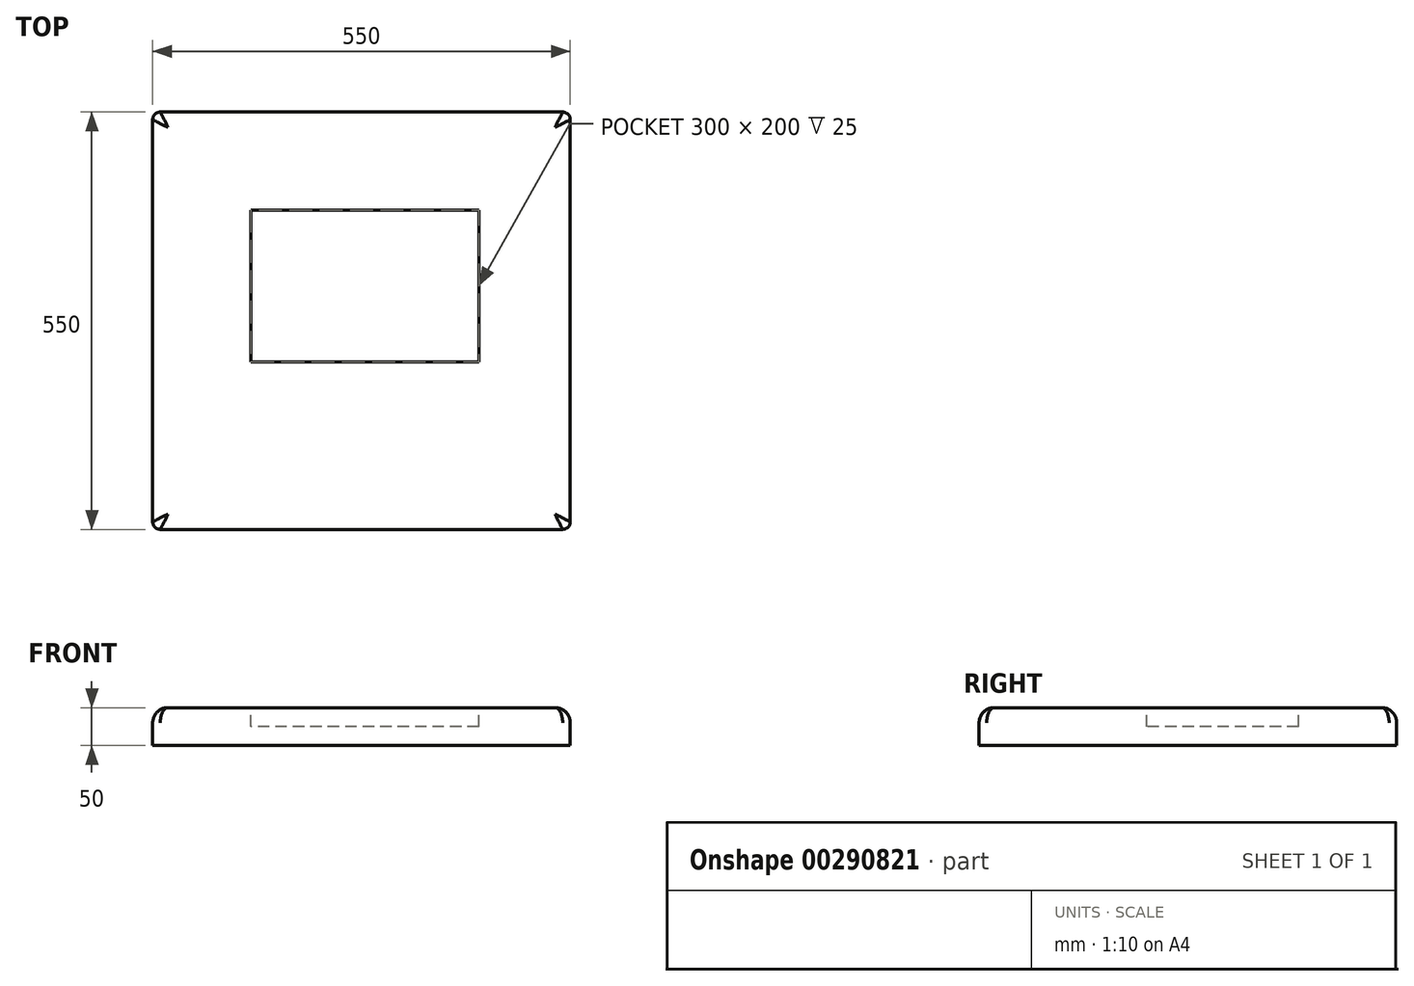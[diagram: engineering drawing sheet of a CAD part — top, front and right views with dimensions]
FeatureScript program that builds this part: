
annotation { "Feature Type Name" : "Feature", "Feature Type Description" : "" }
export const myFeature = defineFeature(function(context is Context, id is Id, definition is map)
    precondition{}
    {
        {
            var Q0;
            Q0=qCreatedBy(makeId("Top.planeOp"),FACE);
            var sketch = newSketch(context, id + "F0", { "sketchPlane" : qUnion([Q0])});
            skLineSegment(sketch, "E0.bottom", {"start": v(-279.6, 410.09) * mm, "end": v(270.4, 410.09) * mm});
            skLineSegment(sketch, "E0.top", {"start": v(-279.6, -139.91) * mm, "end": v(270.4, -139.91) * mm});
            skLineSegment(sketch, "E0.left", {"start": v(-279.6, 410.09) * mm, "end": v(-279.6, -139.91) * mm});
            skLineSegment(sketch, "E0.right", {"start": v(270.4, 410.09) * mm, "end": v(270.4, -139.91) * mm});
            skSolve(sketch);
        }
        {
            var Q0;
            Q0=makeQuery(id+"F0.imprint","IMPRINT",FACE,{"disambiguationData":[TD([[makeQuery(id+"F0.imprint","IMPRINT",EDGE,{"derivedFrom":sQuery(id+"F0.wireOp",EDGE,"E0.bottom")}),-1.0]])]});
            extrude(context, id + "F1", {"entities" : qUnion([Q0]), "depth" : 50 * mm});
        }
        {
            var Q0;
            Q0=makeQuery(id+"F1.opExtrude","CAP_EDGE",EDGE,{"disambiguationData":[OSD([sQuery(id+"F0.wireOp",EDGE,"E0.top")])],"isStart":false});
            var Q1;
            Q1=makeQuery(id+"F1.opExtrude","CAP_EDGE",EDGE,{"disambiguationData":[OSD([sQuery(id+"F0.wireOp",EDGE,"E0.left")])],"isStart":false});
            var Q2;
            Q2=makeQuery(id+"F1.opExtrude","CAP_EDGE",EDGE,{"disambiguationData":[OSD([sQuery(id+"F0.wireOp",EDGE,"E0.bottom")])],"isStart":false});
            var Q3;
            Q3=makeQuery(id+"F1.opExtrude","CAP_EDGE",EDGE,{"disambiguationData":[OSD([sQuery(id+"F0.wireOp",EDGE,"E0.right")])],"isStart":false});
            fillet(context, id + "F2", {"entities" : qUnion([Q0, Q1, Q2, Q3]), "radius" : 20 * mm, "tangentPropagation" : true, "allowEdgeOverflow" : false});
        }
        {
            var Q0;
            Q0=makeQuery(id+"F1.opExtrude","SWEPT_EDGE",EDGE,{"disambiguationData":[OSD([sQuery(id+"F0.wireOp",EDGE,"E0.bottom"),sQuery(id+"F0.wireOp",EDGE,"E0.right")])]});
            var Q1;
            Q1=makeQuery(id+"F2.opFillet","BLEND_EDGE",EDGE,{"blendedFrom":[makeQuery(id+"F1.opExtrude","CAP_EDGE",EDGE,{"disambiguationData":[OSD([sQuery(id+"F0.wireOp",EDGE,"E0.bottom")])],"isStart":false}),makeQuery(id+"F1.opExtrude","CAP_EDGE",EDGE,{"disambiguationData":[OSD([sQuery(id+"F0.wireOp",EDGE,"E0.right")])],"isStart":false})],"blendedInto":[]});
            var Q2;
            Q2=makeQuery(id+"F1.opExtrude","SWEPT_EDGE",EDGE,{"disambiguationData":[OSD([sQuery(id+"F0.wireOp",EDGE,"E0.top"),sQuery(id+"F0.wireOp",EDGE,"E0.right")])]});
            var Q3;
            Q3=makeQuery(id+"F2.opFillet","BLEND_EDGE",EDGE,{"blendedFrom":[makeQuery(id+"F1.opExtrude","CAP_EDGE",EDGE,{"disambiguationData":[OSD([sQuery(id+"F0.wireOp",EDGE,"E0.top")])],"isStart":false}),makeQuery(id+"F1.opExtrude","CAP_EDGE",EDGE,{"disambiguationData":[OSD([sQuery(id+"F0.wireOp",EDGE,"E0.right")])],"isStart":false})],"blendedInto":[]});
            var Q4;
            Q4=makeQuery(id+"F1.opExtrude","SWEPT_EDGE",EDGE,{"disambiguationData":[OSD([sQuery(id+"F0.wireOp",EDGE,"E0.top"),sQuery(id+"F0.wireOp",EDGE,"E0.left")])]});
            var Q5;
            Q5=makeQuery(id+"F2.opFillet","BLEND_EDGE",EDGE,{"blendedFrom":[makeQuery(id+"F1.opExtrude","CAP_EDGE",EDGE,{"disambiguationData":[OSD([sQuery(id+"F0.wireOp",EDGE,"E0.top")])],"isStart":false}),makeQuery(id+"F1.opExtrude","CAP_EDGE",EDGE,{"disambiguationData":[OSD([sQuery(id+"F0.wireOp",EDGE,"E0.left")])],"isStart":false})],"blendedInto":[]});
            var Q6;
            Q6=makeQuery(id+"F1.opExtrude","SWEPT_EDGE",EDGE,{"disambiguationData":[OSD([sQuery(id+"F0.wireOp",EDGE,"E0.bottom"),sQuery(id+"F0.wireOp",EDGE,"E0.left")])]});
            var Q7;
            Q7=makeQuery(id+"F2.opFillet","BLEND_EDGE",EDGE,{"blendedFrom":[makeQuery(id+"F1.opExtrude","CAP_EDGE",EDGE,{"disambiguationData":[OSD([sQuery(id+"F0.wireOp",EDGE,"E0.bottom")])],"isStart":false}),makeQuery(id+"F1.opExtrude","CAP_EDGE",EDGE,{"disambiguationData":[OSD([sQuery(id+"F0.wireOp",EDGE,"E0.left")])],"isStart":false})],"blendedInto":[]});
            fillet(context, id + "F3", {"entities" : qUnion([Q0, Q1, Q2, Q3, Q4, Q5, Q6, Q7]), "radius" : 10 * mm, "tangentPropagation" : true, "allowEdgeOverflow" : false});
        }
        {
            var Q0;
            Q0=makeQuery(id+"F1.opExtrude","CAP_FACE",FACE,{"disambiguationData":[OSD([sQuery(id+"F0.wireOp",EDGE,"E0.bottom"),sQuery(id+"F0.wireOp",EDGE,"E0.top"),sQuery(id+"F0.wireOp",EDGE,"E0.left"),sQuery(id+"F0.wireOp",EDGE,"E0.right")])],"isStart":false});
            var sketch = newSketch(context, id + "F4", { "sketchPlane" : qUnion([Q0])});
            skLineSegment(sketch, "E1.bottom", {"start": v(150, 280.97) * mm, "end": v(-150, 280.97) * mm});
            skLineSegment(sketch, "E1.top", {"start": v(150, 80.97) * mm, "end": v(-150, 80.97) * mm});
            skLineSegment(sketch, "E1.left", {"start": v(150, 280.97) * mm, "end": v(150, 80.97) * mm});
            skLineSegment(sketch, "E1.right", {"start": v(-150, 280.97) * mm, "end": v(-150, 80.97) * mm});
            skPoint(sketch, "E1.middle", {"position": v(0, 180.97) * mm});
            skSolve(sketch);
        }
        {
            var Q0;
            Q0 = qSketchRegion(id + "F4", true);
            extrude(context, id + "F5", {"entities" : qUnion([Q0]), "operationType" : NewBodyOperationType.REMOVE, "oppositeDirection" : true, "depth" : 25 * mm});
        }
    });
